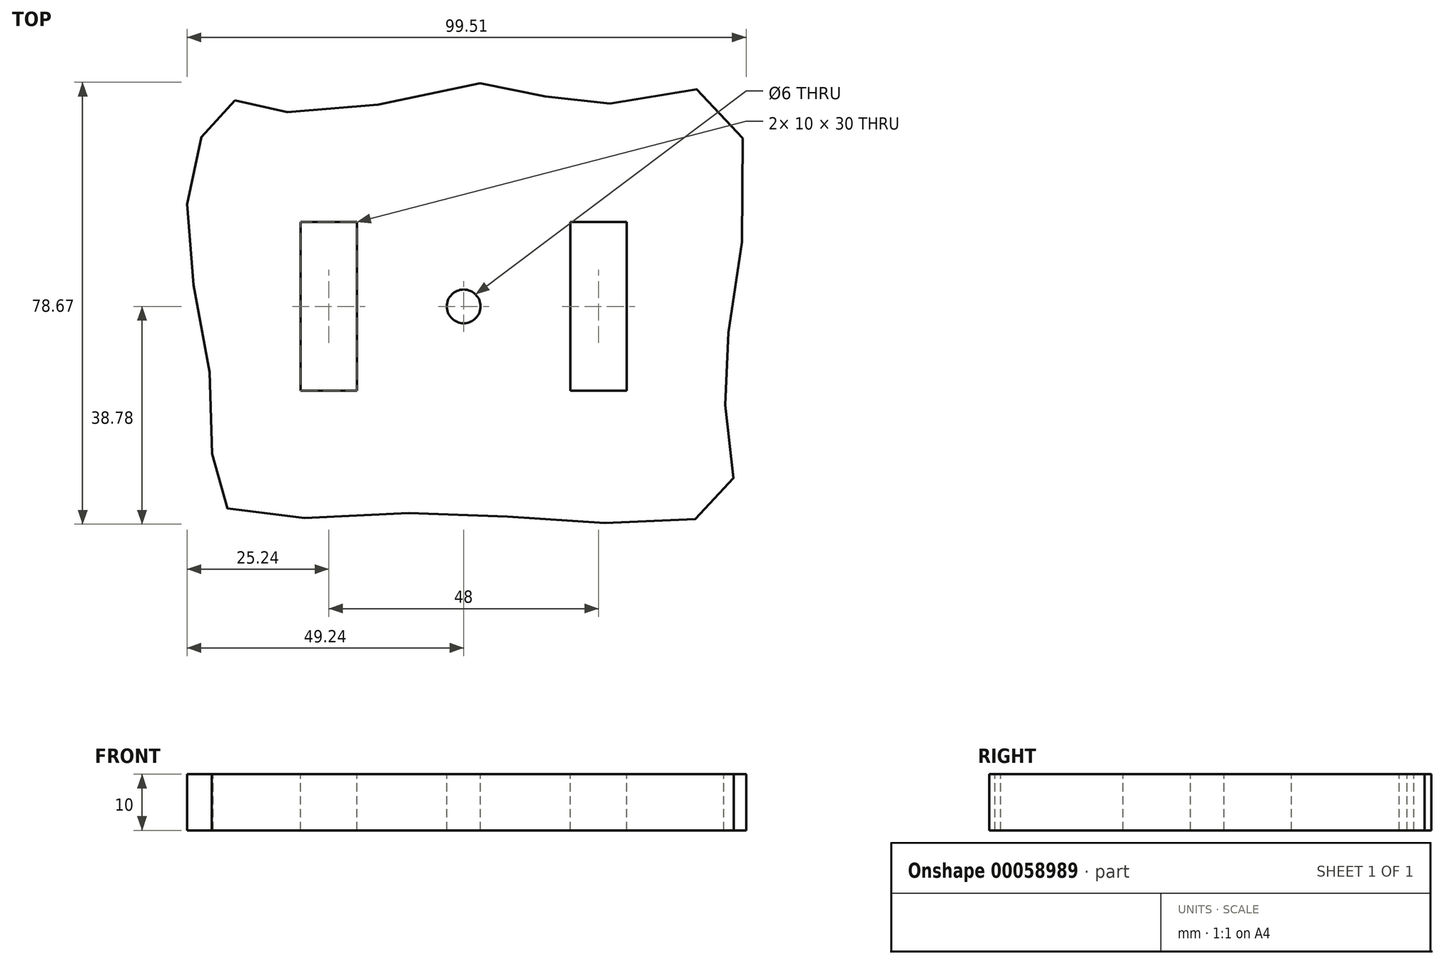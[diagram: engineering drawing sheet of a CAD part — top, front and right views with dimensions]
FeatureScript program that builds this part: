
annotation { "Feature Type Name" : "Feature", "Feature Type Description" : "" }
export const myFeature = defineFeature(function(context is Context, id is Id, definition is map)
    precondition{}
    {
        {
            var Q0;
            Q0=qCreatedBy(makeId("Top.planeOp"),FACE);
            var sketch = newSketch(context, id + "F0", { "sketchPlane" : qUnion([Q0])});
            skLineSegment(sketch, "E0.bottom", {"start": v(-40, 30) * mm, "end": v(40, 30) * mm});
            skLineSegment(sketch, "E0.top", {"start": v(-40, -30) * mm, "end": v(40, -30) * mm});
            skLineSegment(sketch, "E0.left", {"start": v(-40, 30) * mm, "end": v(-40, -30) * mm});
            skLineSegment(sketch, "E0.right", {"start": v(40, 30) * mm, "end": v(40, -30) * mm});
            skPoint(sketch, "E0.middle", {"position": v(0, 0) * mm});
            skSolve(sketch);
        }
        {
            var Q0;
            Q0 = qSketchRegion(id + "F0", true);
            extrude(context, id + "F1", {"entities" : qUnion([Q0]), "depth" : 10 * mm});
        }
        {
            var Q0;
            Q0=makeQuery(id+"F1.opExtrude","CAP_FACE",FACE,{"disambiguationData":[OSD([sQuery(id+"F0.wireOp",EDGE,"E0.bottom"),sQuery(id+"F0.wireOp",EDGE,"E0.top"),sQuery(id+"F0.wireOp",EDGE,"E0.left"),sQuery(id+"F0.wireOp",EDGE,"E0.right")])],"isStart":false});
            var sketch = newSketch(context, id + "F2", { "sketchPlane" : qUnion([Q0])});
            skLineSegment(sketch, "E1.bottom", {"start": v(-29, 15) * mm, "end": v(-19, 15) * mm});
            skLineSegment(sketch, "E1.top", {"start": v(-29, -15) * mm, "end": v(-19, -15) * mm});
            skLineSegment(sketch, "E1.left", {"start": v(-29, 15) * mm, "end": v(-29, -15) * mm});
            skLineSegment(sketch, "E1.right", {"start": v(-19, 15) * mm, "end": v(-19, -15) * mm});
            skPoint(sketch, "E1.middle", {"position": v(-24, 0) * mm});
            skLineSegment(sketch, "E2.MirrorCS", {"start": v(19, 15) * mm, "end": v(19, -15) * mm});
            skLineSegment(sketch, "E3.MirrorCS", {"start": v(29, 15) * mm, "end": v(29, -15) * mm});
            skLineSegment(sketch, "E4.MirrorCS", {"start": v(29, 15) * mm, "end": v(19, 15) * mm});
            skLineSegment(sketch, "E5.MirrorCS", {"start": v(29, -15) * mm, "end": v(19, -15) * mm});
            skPoint(sketch, "E6.MirrorP", {"position": v(24, 0) * mm});
            skSolve(sketch);
        }
        {
            var Q0;
            Q0 = qSketchRegion(id + "F2", true);
            extrude(context, id + "F3", {"entities" : qUnion([Q0]), "operationType" : NewBodyOperationType.REMOVE, "oppositeDirection" : true, "depth" : 25 * mm});
        }
        {
            var Q0;
            Q0=makeQuery(id+"F1.opExtrude","CAP_FACE",FACE,{"disambiguationData":[OSD([sQuery(id+"F0.wireOp",EDGE,"E0.bottom"),sQuery(id+"F0.wireOp",EDGE,"E0.top"),sQuery(id+"F0.wireOp",EDGE,"E0.left"),sQuery(id+"F0.wireOp",EDGE,"E0.right")])],"isStart":false});
            var sketch = newSketch(context, id + "F4", { "sketchPlane" : qUnion([Q0])});
            skCircle(sketch, "E7", {"center": v(0, 0) * mm, "radius": 3 * mm});
            skSolve(sketch);
        }
        {
            var Q0;
            Q0 = qSketchRegion(id + "F4", true);
            extrude(context, id + "F5", {"entities" : qUnion([Q0]), "operationType" : NewBodyOperationType.REMOVE, "oppositeDirection" : true, "depth" : 25 * mm});
        }
        {
            var Q0;
            Q0=makeQuery(id+"F1.opExtrude","CAP_FACE",FACE,{"disambiguationData":[OSD([sQuery(id+"F0.wireOp",EDGE,"E0.bottom"),sQuery(id+"F0.wireOp",EDGE,"E0.top"),sQuery(id+"F0.wireOp",EDGE,"E0.left"),sQuery(id+"F0.wireOp",EDGE,"E0.right")])],"isStart":false});
            var sketch = newSketch(context, id + "F6", { "sketchPlane" : qUnion([Q0])});
            skFitSpline(sketch, "E8", {"points": [v(-40.68, 36.71) * mm, v(-28.28, 34.2) * mm, v(7.56, 39.81) * mm, v(20.73, 35.55) * mm, v(45.53, 37.49) * mm, v(48.82, 6.1) * mm, v(46.5, -17.14) * mm, v(46.69, -34.77) * mm, v(22.86, -38.45) * mm, v(-14.34, -36.9) * mm, v(-42.81, -35.36) * mm, v(-44.56, -19.47) * mm, v(-48.82, 9) * mm, v(-47.08, 29.16) * mm, v(-40.68, 36.71) * mm]});
            skLineSegment(sketch, "E9.bottom", {"start": v(-40, 30) * mm, "end": v(40, 30) * mm});
            skLineSegment(sketch, "E9.top", {"start": v(-40, -30) * mm, "end": v(40, -30) * mm});
            skLineSegment(sketch, "E9.left", {"start": v(-40, 30) * mm, "end": v(-40, -30) * mm});
            skLineSegment(sketch, "E9.right", {"start": v(40, 30) * mm, "end": v(40, -30) * mm});
            skPoint(sketch, "E9.middle", {"position": v(0, 0) * mm});
            skSolve(sketch);
        }
        {
            var Q0;
            Q0 = qSketchRegion(id + "F6", true);
            extrude(context, id + "F7", {"entities" : qUnion([Q0]), "operationType" : NewBodyOperationType.ADD, "oppositeDirection" : true, "depth" : 10 * mm});
        }
    });
